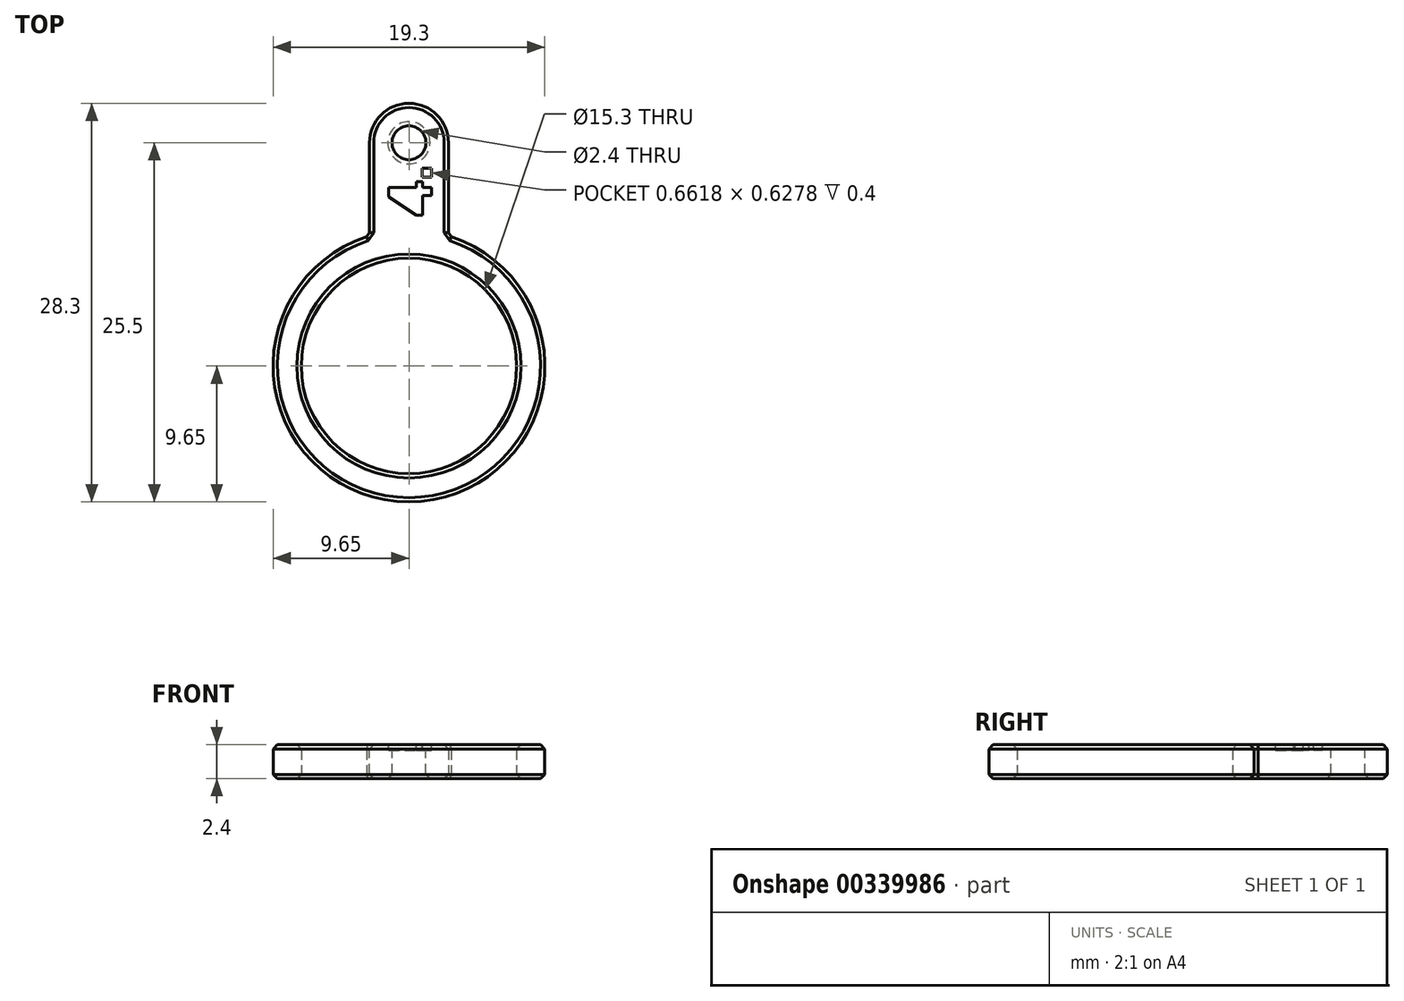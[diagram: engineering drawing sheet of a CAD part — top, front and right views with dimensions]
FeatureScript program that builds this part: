
annotation { "Feature Type Name" : "Feature", "Feature Type Description" : "" }
export const myFeature = defineFeature(function(context is Context, id is Id, definition is map)
    precondition{}
    {
        {
            var Q0;
            Q0=qCreatedBy(makeId("Top.planeOp"),FACE);
            var sketch = newSketch(context, id + "F0", { "sketchPlane" : qUnion([Q0])});
            skCircle(sketch, "E0", {"center": v(0, 0) * mm, "radius": 7.65 * mm});
            skCircle(sketch, "E1", {"center": v(0, 0) * mm, "radius": 9.65 * mm});
            skLineSegment(sketch, "E2.bottom", {"start": v(2.8, 0.65) * mm, "end": v(-2.8, 0.65) * mm});
            skLineSegment(sketch, "E2.top", {"start": v(2.8, 18.65) * mm, "end": v(-2.8, 18.65) * mm});
            skLineSegment(sketch, "E2.left", {"start": v(2.8, 0.65) * mm, "end": v(2.8, 18.65) * mm});
            skLineSegment(sketch, "E2.right", {"start": v(-2.8, 0.65) * mm, "end": v(-2.8, 18.65) * mm});
            skPoint(sketch, "E2.middle", {"position": v(0, 9.65) * mm});
            skSolve(sketch);
        }
        {
            var Q0;
            Q0=qSketchRegion(id+"F0",true);
            extrude(context, id + "F1", {"entities" : qUnion([Q0]), "depth" : 2.4 * mm});
        }
        {
            var Q0;
            Q0=makeQuery(id+"F1.opExtrude","SWEPT_EDGE",EDGE,{"disambiguationData":[OSD([sQuery(id+"F0.wireOp",EDGE,"E2.top"),sQuery(id+"F0.wireOp",EDGE,"E2.right")])]});
            var Q1;
            Q1=makeQuery(id+"F1.opExtrude","SWEPT_EDGE",EDGE,{"disambiguationData":[OSD([sQuery(id+"F0.wireOp",EDGE,"E2.top"),sQuery(id+"F0.wireOp",EDGE,"E2.left")])]});
            fillet(context, id + "F2", {"entities" : qUnion([Q0, Q1]), "radius" : 2.8 * mm, "tangentPropagation" : true, "allowEdgeOverflow" : false});
        }
        {
            var Q0;
            Q0=makeQuery(id+"F1.opExtrude","CAP_FACE",FACE,{"disambiguationData":[OSD([sQuery(id+"F0.wireOp",EDGE,"E0"),sQuery(id+"F0.wireOp",EDGE,"E1"),sQuery(id+"F0.wireOp",EDGE,"E2.top"),sQuery(id+"F0.wireOp",EDGE,"E2.left"),sQuery(id+"F0.wireOp",EDGE,"E2.right")])],"isStart":false});
            var sketch = newSketch(context, id + "F3", { "sketchPlane" : qUnion([Q0])});
            skCircle(sketch, "E3", {"center": v(0, 15.85) * mm, "radius": 1.2 * mm});
            skSolve(sketch);
        }
        {
            var Q0;
            Q0=qSketchRegion(id+"F3",true);
            extrude(context, id + "F4", {"entities" : qUnion([Q0]), "operationType" : NewBodyOperationType.REMOVE, "oppositeDirection" : true, "depth" : 25 * mm});
        }
        {
            var Q0;
            Q0=makeQuery(id+"F4.boolean.opBoolean","COPY",EDGE,{"derivedFrom":makeQuery(id+"F4.opExtrude","CAP_EDGE",EDGE,{"disambiguationData":[OSD([sQuery(id+"F3.wireOp",EDGE,"E3")])],"isStart":true})});
            var Q1;
            Q1=makeQuery(id+"F4.boolean.opBoolean","INTERSECT",EDGE,{"derivedFrom":[makeQuery(id+"F1.opExtrude","CAP_FACE",FACE,{"disambiguationData":[OSD([sQuery(id+"F0.wireOp",EDGE,"E0"),sQuery(id+"F0.wireOp",EDGE,"E1"),sQuery(id+"F0.wireOp",EDGE,"E2.top"),sQuery(id+"F0.wireOp",EDGE,"E2.left"),sQuery(id+"F0.wireOp",EDGE,"E2.right")])],"isStart":true}),makeQuery(id+"F4.opExtrude","SWEPT_FACE",FACE,{"disambiguationData":[OSD([sQuery(id+"F3.wireOp",EDGE,"E3")])]})]});
            var Q2;
            {var subQ0=sQuery(id+"F0.wireOp",EDGE,"E2.right");var subQ1=sQuery(id+"F0.wireOp",EDGE,"E2.top");Q2=makeQuery(id+"F2.opFillet","BLEND_EDGE",EDGE,{"blendedFrom":[makeQuery(id+"F1.opExtrude","SWEPT_EDGE",EDGE,{"disambiguationData":[OSD([subQ1,subQ0])]}),makeQuery(id+"F1.opExtrude","CAP_FACE",FACE,{"disambiguationData":[OSD([sQuery(id+"F0.wireOp",EDGE,"E0"),sQuery(id+"F0.wireOp",EDGE,"E1"),subQ1,sQuery(id+"F0.wireOp",EDGE,"E2.left"),subQ0])],"isStart":true})],"blendedInto":[makeQuery(id+"F1.opExtrude","CAP_FACE",FACE,{"disambiguationData":[OSD([sQuery(id+"F0.wireOp",EDGE,"E0"),sQuery(id+"F0.wireOp",EDGE,"E1"),subQ1,sQuery(id+"F0.wireOp",EDGE,"E2.left"),subQ0])],"isStart":true})]});}
            var Q3;
            {var subQ0=sQuery(id+"F0.wireOp",EDGE,"E2.right");var subQ1=sQuery(id+"F0.wireOp",EDGE,"E2.top");Q3=makeQuery(id+"F2.opFillet","BLEND_EDGE",EDGE,{"blendedFrom":[makeQuery(id+"F1.opExtrude","SWEPT_EDGE",EDGE,{"disambiguationData":[OSD([subQ1,subQ0])]}),makeQuery(id+"F1.opExtrude","CAP_FACE",FACE,{"disambiguationData":[OSD([sQuery(id+"F0.wireOp",EDGE,"E0"),sQuery(id+"F0.wireOp",EDGE,"E1"),subQ1,sQuery(id+"F0.wireOp",EDGE,"E2.left"),subQ0])],"isStart":false})],"blendedInto":[makeQuery(id+"F1.opExtrude","CAP_FACE",FACE,{"disambiguationData":[OSD([sQuery(id+"F0.wireOp",EDGE,"E0"),sQuery(id+"F0.wireOp",EDGE,"E1"),subQ1,sQuery(id+"F0.wireOp",EDGE,"E2.left"),subQ0])],"isStart":false})]});}
            var Q4;
            Q4=makeQuery(id+"F1.opExtrude","CAP_EDGE",EDGE,{"disambiguationData":[OSD([sQuery(id+"F0.wireOp",EDGE,"E1")])],"isStart":false});
            var Q5;
            Q5=makeQuery(id+"F1.opExtrude","CAP_EDGE",EDGE,{"disambiguationData":[OSD([sQuery(id+"F0.wireOp",EDGE,"E1")])],"isStart":true});
            var Q6;
            Q6=makeQuery(id+"F1.opExtrude","SWEPT_EDGE",EDGE,{"disambiguationData":[OSD([sQuery(id+"F0.wireOp",EDGE,"E1"),sQuery(id+"F0.wireOp",EDGE,"E2.left")])]});
            var Q7;
            Q7=makeQuery(id+"F1.opExtrude","SWEPT_EDGE",EDGE,{"disambiguationData":[OSD([sQuery(id+"F0.wireOp",EDGE,"E1"),sQuery(id+"F0.wireOp",EDGE,"E2.right")])]});
            var Q8;
            Q8=makeQuery(id+"F1.opExtrude","CAP_EDGE",EDGE,{"disambiguationData":[OSD([sQuery(id+"F0.wireOp",EDGE,"E0")])],"isStart":true});
            var Q9;
            Q9=makeQuery(id+"F1.opExtrude","CAP_EDGE",EDGE,{"disambiguationData":[OSD([sQuery(id+"F0.wireOp",EDGE,"E0")])],"isStart":false});
            chamfer(context, id + "F5", {"entities" : qUnion([Q0, Q1, Q2, Q3, Q4, Q5, Q6, Q7, Q8, Q9]), "width" : 0.3 * mm, "tangentPropagation" : true});
        }
        {
            var Q0;
            Q0=makeQuery(id+"F1.opExtrude","CAP_FACE",FACE,{"disambiguationData":[OSD([sQuery(id+"F0.wireOp",EDGE,"E0"),sQuery(id+"F0.wireOp",EDGE,"E1"),sQuery(id+"F0.wireOp",EDGE,"E2.top"),sQuery(id+"F0.wireOp",EDGE,"E2.left"),sQuery(id+"F0.wireOp",EDGE,"E2.right")])],"isStart":false});
            var sketch = newSketch(context, id + "F6", { "sketchPlane" : qUnion([Q0])});
            skText(sketch, "E4", { "text": "4.", "fontName": "Arimo-Bold.ttf"});
            skLineSegment(sketch, "E5", {"start": v(0, 10.64) * mm, "end": v(0, 0) * mm});
            skPoint(sketch, "E5.endSnap0", {"position": v(0, 10.64) * mm});
            const initialGuessF6  = {"E4": [0.0016, 0.01064, 0, 1, 0.0032]};
            skSetInitialGuess(sketch, initialGuessF6);
            skSolve(sketch);
        }
        {
            var Q0;
            Q0=qSketchRegion(id+"F6",true);
            var Q1;
            Q1=makeQuery(id+"F6.imprint","IMPRINT",FACE,{"disambiguationData":[TD([[makeQuery(id+"F6.imprint","IMPRINT",EDGE,{"derivedFrom":sQuery(id+"F6.wireOp",EDGE,"E4.sketch_text.stroke-11")}),1.0]])]});
            extrude(context, id + "F7", {"entities" : qUnion([Q0, Q1]), "operationType" : NewBodyOperationType.REMOVE, "oppositeDirection" : true, "depth" : 0.4 * mm});
        }
    });
